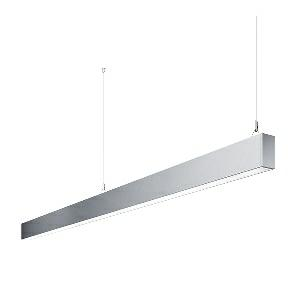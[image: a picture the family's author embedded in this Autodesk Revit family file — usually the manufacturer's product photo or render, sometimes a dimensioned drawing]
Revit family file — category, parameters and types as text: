
# Revit family: idoo_line_-_ilp_6000_830_d_end_00805750_bb35
name_source: partatom
category: Lighting Fixtures
units: mm (PartAtom-declared; Revit-internal decimal feet)

## family parameters
Cut with Voids When Loaded = No
Host = Face
Light Source = No
Part Type = Normal
Room Calculation Point = No
Round Connector Dimension = Use Diameter
Shared = No

## types (1)
- IDOO.line - ILP 6000/830/D END (1 x LED, 6000 lm, 3000K)
    Apparent Load = 46 VA
    Approval mark = CE
    CIE Flux Codes = 66 91 98 40 100
    Color Rendering = 80-89
    Color Temperature = 3000K
    Control Gear = Electronic ballast
    Default Elevation = 1800 mm
    Description = ILP 6000/830/D|Suspended luminaire|light source: LED|connected load: 220-240 V, 50/60 Hz|Power consumption: approx. 46 W|standby: approx. 0,15|luminous flux: 6000 lm|luminous efficacy: 130 lm/W|light distribution: Direct/indirect|direct ratio: approx. 40 %|colour temperature: Warm white, ca. 3000 K|color rendering index (CRI): >= 80|chromaticity tolerance:  3 SDCM|System of protection: IP 40|technology: Continuously dimmable|luminaire body|material: Sectional aluminium|colour: Silver|lamp cover: Acrylic (PMMA), Clear|mains lead: 1,0 m With free stranded wires|Fastening: Steel cable 0.3 - 0.7 m|glare control: Prism aperture|luminance(L65): <= 2700 cd/m|unified glare rating(4H 8H): <=  16|special features: DALI Load 1x, TouchDIM - dimming via standard switch, Through-wired, up to 18 m on one mains connection, Flicker-free, Suitable as emergency lighting, Mechanical and electrical connection of the individual modules without tools|
    Frequency = 50 Hz
    Height = 110 mm
    Lamp = 1 x LED
    Lamp Light Flux = 6000 lm
    Lamp count = 1
    Length = 2250 mm
    Luminous efficacy = 130 lm/W
    Manufacturer = Waldmann
    ModVariant = No
    Model = 00805750
    Mounting Place = Ceiling
    Mounting Type = Pendant
    Number of Poles = 1
    OnlyDefault = Yes
    Power Factor = 1
    Product Name = IDOO.line - ILP 6000/830/D END
    Product group = Suspended luminaire
    ProductGroupID = 9
    Protection Class = Protection class I
    Protection Degree = IP 40
    RLX_Detail_Level = 1
    RLX_Emergency_Light_Flux = 0 lm
    RLX_Emergency_Type = 0
    RLX_Emergency_Type_DB = No
    RlxData = <blob elided: 22849 chars, md5=567354c6>
    Socket = socket
    Standby Power = 0 W
    System Light Flux = 6000 lm
    System Power = 46 W
    Type Comments = Product without accessories
    Type Image = 113318000-00692621.jpg
    URL = http://relux.com
    VarID = ---
    Voltage = 230 V
    Voltage Range = 220-240 V
    Weight = 0.00 kg
    Width = 60 mm  [stored 0.19685 ft]

note: [stored X ft] marks values corroborated as IEEE doubles in the binary element streams (Revit-internal decimal feet)

## geometry (parser evidence)
native form markers: Blend x4, Sweep x15
no freeform markers — native parametric forms only
